# Revit family: Kitchen_Taps-Mixers_hansgrohe_72841XXX-Talis-M54-F21-Shut-off-valve-fo_
name_source: partatom
category: Plumbing Fixtures
revit_build: Autodesk Revit 2015 (Build: 20140903_1530(x64)
units: mm (PartAtom-declared; Revit-internal decimal feet)

## types (3) — shared parameters
BIMobject category = Taps & Mixers
BIMobject category code = kitchen-taps
BIMobject main category = Kitchen
BIMobject main category code = kitchen
Brand url = http://www.hansgrohe-int.com
Design country = Germany
Edition number = 1
GTIN code = https://4059625293218
IFC Classification = Sanitary Terminal
Installation instructions = https://www.hansgrohe.com
Manufacturer country = Germany
Manufacturer name = hansgrohe
Material main = Chrome
Product Guid = e0c0e07f-45fd-431d-bfbf-33aa5c2a7bc3
Product SKU = 72841XXX
Product data url = https://bimobject.com
Product family = Talis M54
Product group = Supplies
Product name = 72841XXX Talis M54 F21-  Shut-off valve for concealed installation
Product url = https://www.hansgrohe.com
QR code = http://bimobject.com
Technical description = https://www.hansgrohe.com

## type names (no varying parameters)
- 000 Chrome
- 670 Matte Black
- 800 Stainless Steel Finish

## geometry (parser evidence)
native form markers: Sweep x3
no freeform markers — native parametric forms only
